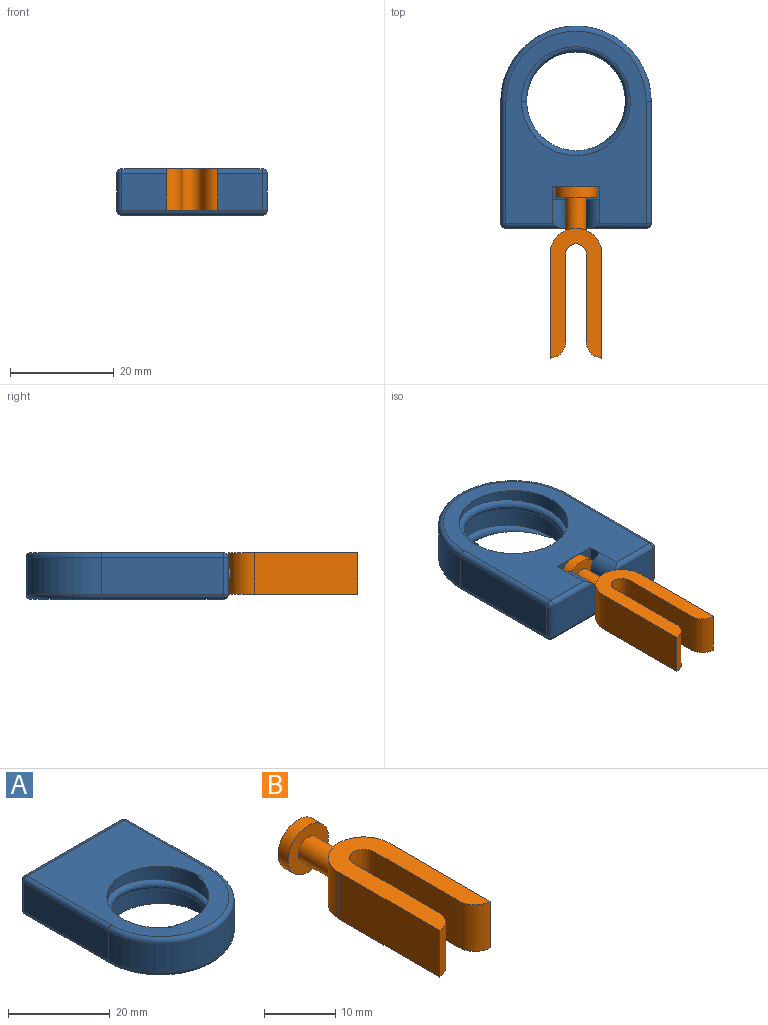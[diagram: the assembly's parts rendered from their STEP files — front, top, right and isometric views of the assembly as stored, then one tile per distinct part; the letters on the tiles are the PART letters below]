
ASSEMBLY  parts=2 mates=1
PART A: 34 faces, bbox 31.7x40.5x12.3 mm
  f0: plane 8x2.5mm, normal (-1,0,0), area 20mm2, adj f9,f11,f12,f13
  f1: plane 8x2.5mm, normal (1,0,0), area 20mm2, adj f9,f11,f12,f13
  f2: plane 27x7mm, normal (0,1,0), area 169.8mm2, adj f14,f15,f16,f17,f18,f22,f23,f24
  f3: bspline ~24.25x21mm, area 260.2mm2, adj f4,f8,f10
  f4: cylinder r=10.5mm len=21mm, axis (0,0,-1), area 417.9mm2, adj f3,f8,f9,f10
  f5: plane 23.5x7mm, normal (-1,0,0), area 164.5mm2, adj f6,f25,f30,f33
  f6: cylinder r=14.5mm len=29mm, axis (0,0,-1), area 318.9mm2, adj f5,f7,f21,f31
  f7: plane 23.5x7mm, normal (1,0,0), area 164.5mm2, adj f6,f19,f22,f28
  f8: plane 37x27mm, normal (0,0,1), area 590.9mm2, adj f3,f4,f19,f21,f24,f25
  f9: plane 37x27mm, normal (0,0,-1), area 511.4mm2, adj f0,f1,f4,f11,f16,f17,f23,f28
  f10: plane 2.28x1.28mm, normal (0,1,0), area 1.6mm2, adj f3,f4
  f11: plane 9x8mm, normal (0,1,0), area 72mm2, adj f0,f1,f9,f13
  f12: plane 9x8mm, normal (0,-1,0), area 46mm2, adj f0,f1,f13,f14,f15,f16,f17,f18
  f13: plane 9x2.5mm, normal (0,0,-1), area 22.5mm2, adj f0,f1,f11,f12
  f14: cylinder r=2mm len=5.5mm, axis (0,1,0), area 34.6mm2, adj f2,f12,f15,f18
  f15: plane 5.5x1mm, normal (1,0,0), area 5.5mm2, adj f2,f12,f14,f16
  f16: cylinder r=3.05mm len=5.5mm, axis (0,1,0), area 22.3mm2, adj f2,f9,f12,f15,f29
  f17: cylinder r=3.05mm len=5.5mm, axis (0,1,0), area 22.3mm2, adj f2,f9,f12,f18,f23
  f18: plane 5.5x1mm, normal (-1,0,0), area 5.5mm2, adj f2,f12,f14,f17
  f19: cylinder r=1mm len=23.5mm, axis (0,-1,0), area 36.9mm2, adj f7,f8,f20,f21
  f20: sphere r=1mm, area 1.6mm2, adj f19,f22,f24
  f21: torus R=13.5mm, axis (0,0,1), area 69.8mm2, adj f6,f8,f19,f25
  f22: cylinder r=1mm len=7mm, axis (0,0,-1), area 11mm2, adj f2,f7,f20,f26
  f23: cylinder r=1mm len=10.75mm, axis (-1,0,0), area 15.5mm2, adj f2,f9,f17,f26
  f24: cylinder r=1mm len=27mm, axis (1,0,0), area 42.4mm2, adj f2,f8,f20,f27
  f25: cylinder r=1mm len=23.5mm, axis (0,1,0), area 36.9mm2, adj f5,f8,f21,f27
  f26: sphere r=1mm, area 1.6mm2, adj f22,f23,f28
  f27: sphere r=1mm, area 1.6mm2, adj f24,f25,f30
  f28: cylinder r=1mm len=23.5mm, axis (0,1,0), area 36.9mm2, adj f7,f9,f26,f31
  f29: cylinder r=1mm len=10.75mm, axis (-1,0,0), area 15.5mm2, adj f2,f9,f16,f32
  f30: cylinder r=1mm len=7mm, axis (0,0,-1), area 11mm2, adj f2,f5,f27,f32
  f31: torus R=13.5mm, axis (0,0,1), area 69.8mm2, adj f6,f9,f28,f33
  f32: sphere r=1mm, area 1.6mm2, adj f29,f30,f33
  f33: cylinder r=1mm len=23.5mm, axis (0,-1,0), area 36.9mm2, adj f5,f9,f31,f32
PART B: 14 faces, bbox 10x33x8 mm
  f0: plane 8x8mm, normal (0,1,0), area 50.3mm2, adj f11
  f1: plane 8x8mm, normal (0,-1,0), area 37.7mm2, adj f10,f11
  f2: cylinder r=5mm len=10mm, axis (0,0,-1), area 112.8mm2, adj f6,f7,f8,f9,f10
  f3: plane 17x8mm, normal (1,0,0), area 136mm2, adj f4,f8,f9,f13
  f4: cylinder r=2mm len=8mm, axis (0,0,-1), area 50.3mm2, adj f3,f5,f8,f9
  f5: plane 17x8mm, normal (-1,0,0), area 136mm2, adj f4,f8,f9,f12
  f6: plane 20x8mm, normal (1,0,0), area 160mm2, adj f2,f8,f9,f12
  f7: plane 20x8mm, normal (-1,0,0), area 160mm2, adj f2,f8,f9,f13
  f8: plane 25x10mm, normal (0,0,1), area 149.1mm2, adj f2,f3,f4,f5,f6,f7,f12,f13
  f9: plane 25x10mm, normal (0,0,-1), area 149.1mm2, adj f2,f3,f4,f5,f6,f7,f12,f13
  f10: cylinder r=2mm len=6.42mm, axis (0,1,0), area 78mm2, adj f1,f2
  f11: cylinder r=4mm len=8mm, axis (0,-1,0), area 50.3mm2, adj f0,f1
  f12: cylinder r=3mm len=8mm, axis (0,0,-1), area 37.7mm2, adj f5,f6,f8,f9
  f13: cylinder r=3mm len=8mm, axis (0,0,1), area 37.7mm2, adj f3,f7,f8,f9
PLACE A rot(axis=(1,0,0),180deg) t=(0,0,10)mm
PLACE B t=(0,-18.5,2)mm
MATE revolute A.f14 <-> B.f11  axis (0,-1,0) through (0,-16.5,6)mm
